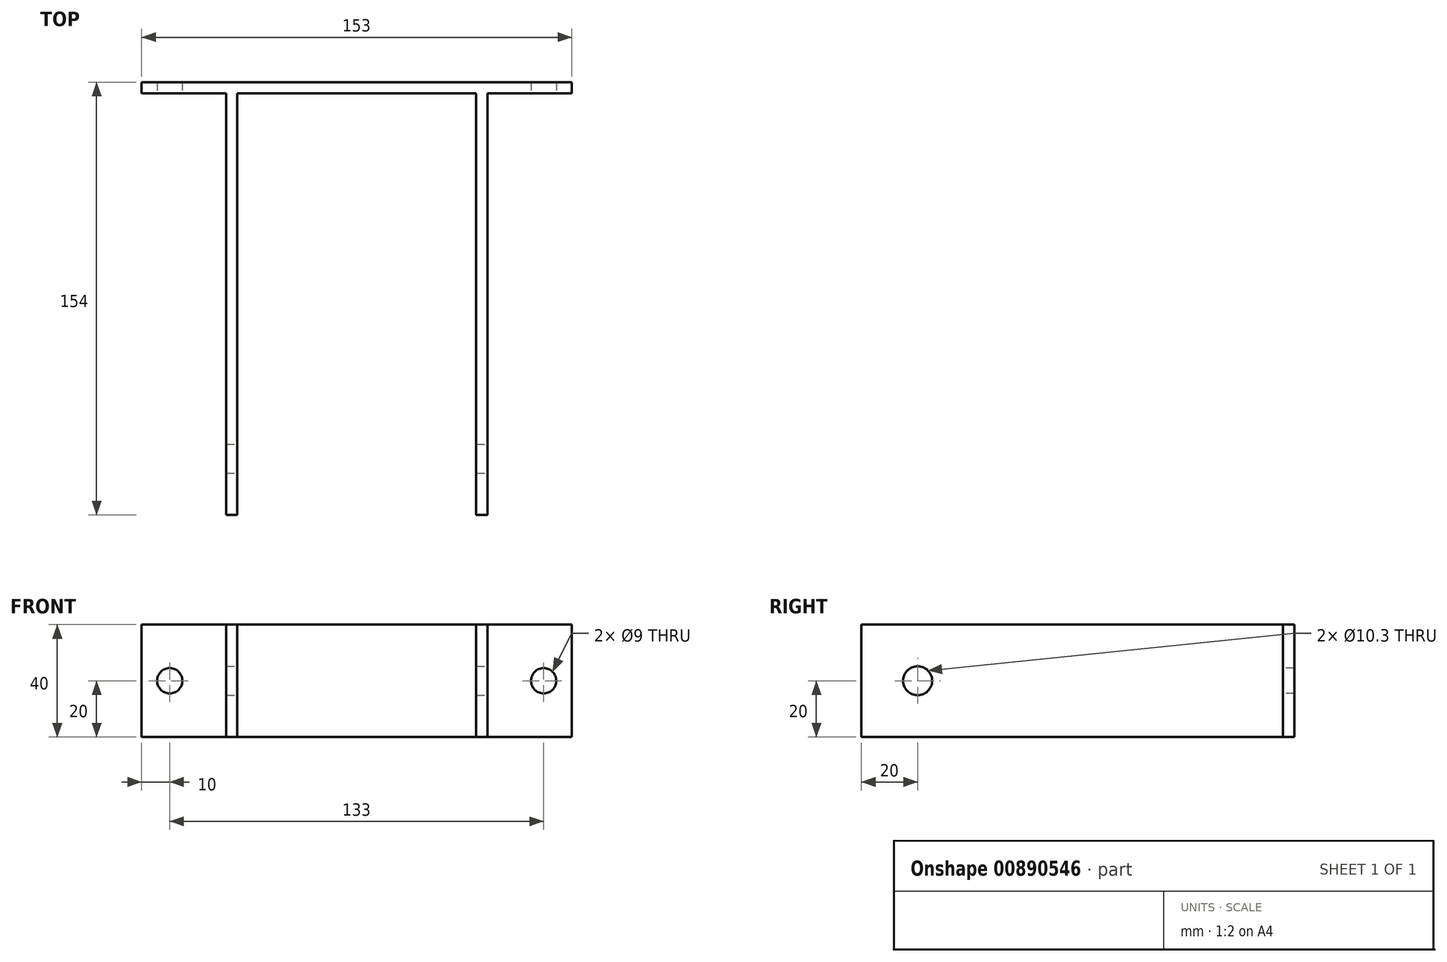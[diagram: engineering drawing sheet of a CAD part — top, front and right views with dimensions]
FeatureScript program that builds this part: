
annotation { "Feature Type Name" : "Feature", "Feature Type Description" : "" }
export const myFeature = defineFeature(function(context is Context, id is Id, definition is map)
    precondition{}
    {
        {
            var Q0;
            Q0=qCreatedBy(makeId("Front.planeOp"),FACE);
            var sketch = newSketch(context, id + "F0", { "sketchPlane" : qUnion([Q0])});
            skLineSegment(sketch, "E0.bottom", {"start": v(0, 0) * mm, "end": v(153, 0) * mm});
            skLineSegment(sketch, "E0.top", {"start": v(0, 40) * mm, "end": v(153, 40) * mm});
            skLineSegment(sketch, "E0.left", {"start": v(0, 0) * mm, "end": v(0, 40) * mm});
            skLineSegment(sketch, "E0.right", {"start": v(153, 0) * mm, "end": v(153, 40) * mm});
            skSolve(sketch);
        }
        {
            var Q0;
            Q0 = qSketchRegion(id + "F0", true);
            extrude(context, id + "F1", {"entities" : qUnion([Q0]), "depth" : 4 * mm, "offsetDistance" : 25 * mm});
        }
        {
            var Q0;
            Q0=makeQuery(id+"F1.opExtrude","CAP_FACE",FACE,{"disambiguationData":[OSD([sQuery(id+"F0.wireOp",EDGE,"E0.bottom"),sQuery(id+"F0.wireOp",EDGE,"E0.top"),sQuery(id+"F0.wireOp",EDGE,"E0.left"),sQuery(id+"F0.wireOp",EDGE,"E0.right")])],"isStart":false});
            var sketch = newSketch(context, id + "F2", { "sketchPlane" : qUnion([Q0])});
            skLineSegment(sketch, "E1.bottom", {"start": v(30, 40) * mm, "end": v(34, 40) * mm});
            skLineSegment(sketch, "E1.top", {"start": v(30, 0) * mm, "end": v(34, 0) * mm});
            skLineSegment(sketch, "E1.left", {"start": v(30, 40) * mm, "end": v(30, 0) * mm});
            skLineSegment(sketch, "E1.right", {"start": v(34, 40) * mm, "end": v(34, 0) * mm});
            skLineSegment(sketch, "E2.bottom", {"start": v(119, 40) * mm, "end": v(123, 40) * mm});
            skLineSegment(sketch, "E2.top", {"start": v(119, 0) * mm, "end": v(123, 0) * mm});
            skLineSegment(sketch, "E2.left", {"start": v(119, 40) * mm, "end": v(119, 0) * mm});
            skLineSegment(sketch, "E2.right", {"start": v(123, 40) * mm, "end": v(123, 0) * mm});
            skSolve(sketch);
        }
        {
            var Q0;
            Q0 = qSketchRegion(id + "F2", true);
            extrude(context, id + "F3", {"entities" : qUnion([Q0]), "operationType" : NewBodyOperationType.ADD, "depth" : (40 + 80 + 30) * mm, "offsetDistance" : 25 * mm});
        }
        {
            var Q0;
            {var subQ0=sQuery(id+"F0.wireOp",EDGE,"E0.right");var subQ1=sQuery(id+"F0.wireOp",EDGE,"E0.top");var subQ2=sQuery(id+"F0.wireOp",EDGE,"E0.bottom");Q0=makeQuery(id+"F3.boolean.opBoolean","SPLIT",FACE,{"disambiguationData":[TD([makeQuery(id+"F1.opExtrude","SWEPT_FACE",FACE,{"disambiguationData":[OSD([subQ0])]})])],"derivedFrom":makeQuery(id+"F1.opExtrude","CAP_FACE",FACE,{"disambiguationData":[OSD([subQ2,subQ1,sQuery(id+"F0.wireOp",EDGE,"E0.left"),subQ0])],"isStart":false})});}
            var sketch = newSketch(context, id + "F4", { "sketchPlane" : qUnion([Q0])});
            skCircle(sketch, "E3", {"center": v(143, 20) * mm, "radius": 4.5 * mm});
            skCircle(sketch, "E4", {"center": v(10, 20) * mm, "radius": 4.5 * mm});
            skSolve(sketch);
        }
        {
            var Q0;
            Q0 = qSketchRegion(id + "F4", true);
            extrude(context, id + "F5", {"entities" : qUnion([Q0]), "operationType" : NewBodyOperationType.REMOVE, "oppositeDirection" : true, "depth" : 25 * mm, "offsetDistance" : 25 * mm});
        }
        {
            var Q0;
            Q0=makeQuery(id+"F3.opExtrude","SWEPT_FACE",FACE,{"disambiguationData":[OSD([sQuery(id+"F2.wireOp",EDGE,"E2.right")])]});
            var sketch = newSketch(context, id + "F6", { "sketchPlane" : qUnion([Q0])});
            skCircle(sketch, "E5", {"center": v(-134, 20) * mm, "radius": 5.15 * mm});
            skSolve(sketch);
        }
        {
            var Q0;
            Q0 = qSketchRegion(id + "F6", true);
            extrude(context, id + "F7", {"entities" : qUnion([Q0]), "operationType" : NewBodyOperationType.REMOVE, "endBound" : BoundingType.THROUGH_ALL, "oppositeDirection" : true, "depth" : 25 * mm, "offsetDistance" : 25 * mm});
        }
    });
